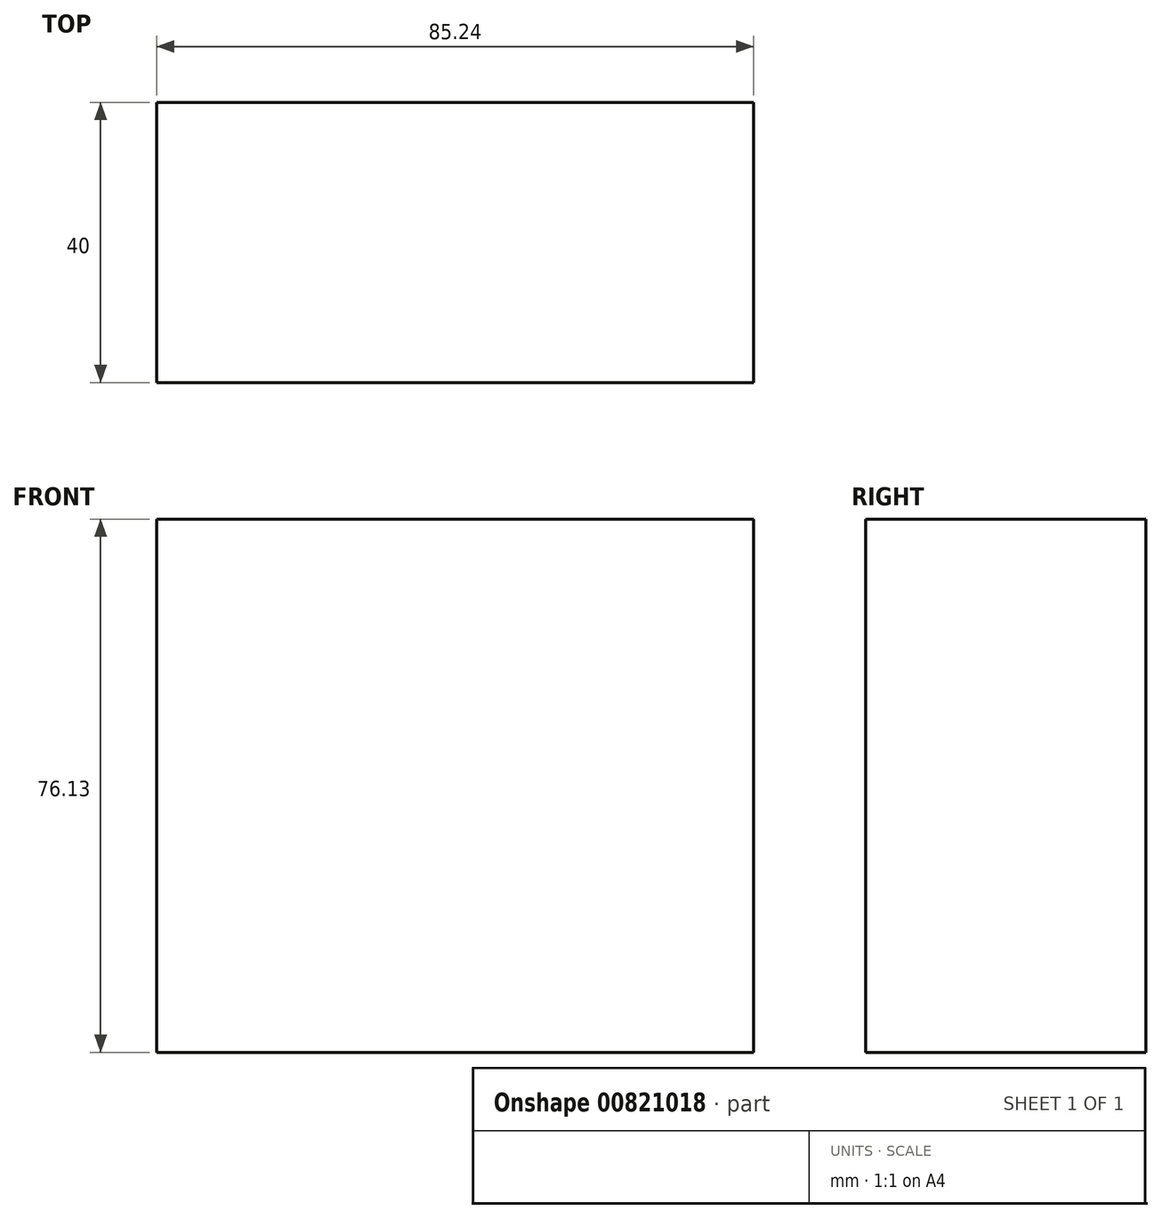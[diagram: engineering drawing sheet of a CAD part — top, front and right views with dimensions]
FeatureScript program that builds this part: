
annotation { "Feature Type Name" : "Feature", "Feature Type Description" : "" }
export const myFeature = defineFeature(function(context is Context, id is Id, definition is map)
    precondition{}
    {
        {
            var Q0;
            Q0=qCreatedBy(makeId("Front.planeOp"),FACE);
            var sketch = newSketch(context, id + "F0", { "sketchPlane" : qUnion([Q0])});
            skLineSegment(sketch, "E0.bottom", {"start": v(-60.54, 57.5) * mm, "end": v(24.7, 57.5) * mm});
            skLineSegment(sketch, "E0.top", {"start": v(-60.54, -18.63) * mm, "end": v(24.7, -18.63) * mm});
            skLineSegment(sketch, "E0.left", {"start": v(-60.54, 57.5) * mm, "end": v(-60.54, -18.63) * mm});
            skLineSegment(sketch, "E0.right", {"start": v(24.7, 57.5) * mm, "end": v(24.7, -18.63) * mm});
            skSolve(sketch);
        }
        {
            var Q0;
            Q0 = qSketchRegion(id + "F0", true);
            var sketch = newSketch(context, id + "F1", { "sketchPlane" : qUnion([Q0])});
            skSolve(sketch);
        }
        {
            var Q0;
            Q0=makeQuery(id+"F1.imprint","IMPRINT",FACE,{"disambiguationData":[TD([[makeQuery(id+"F1.imprint","IMPRINT",EDGE,{"derivedFrom":makeQuery(id+"F0.imprint","IMPRINT",EDGE,{"derivedFrom":sQuery(id+"F0.wireOp",EDGE,"E0.bottom")})}),-1.0]])]});
            extrude(context, id + "F2", {"entities" : qUnion([Q0]), "depth" : 40 * mm, "offsetDistance" : 25 * mm});
        }
    });
